# Revit family: Platinum_BC_iPlus_8_MR
name_source: partatom
category: Equipos mecánicos
units: mm (PartAtom-declared; Revit-internal decimal feet)

## family parameters
Compartido = No
Corte con vacíos al cargar = No
Cota de conector redondo = Diámetro de uso
Número OmniClass = 23.75.10.21
Punto de cálculo de habitación = No
Se basa en plano de trabajo = No
Siempre vertical = Sí
Tipo de pieza = Normal
Título OmniClass = Heat Pumps

## types (1)
- Platinum BC iPLUS 8 MR (U.E)
    Altura = 943 mm  [stored 3.09383 ft]
    Anchura = 950 mm
    Blanco = Color RGB 216-216-216
    Cantidad Compresores = 1
    Cantidad de Ventiladores = 1
    Capacidad Calorifica (kW) = 7.9
    Capacidad frigorifica (kW) = 7.9
    Caudal Aire (m3/min) = 55
    Código de montaje = 7609926
    Descripción = Platinum BC iPlus 8MR
    Diametro drenaje = 32 mm
    Diametro gas refrigerante = 15.9 mm
    Diametro liquido refrigerante = 9.53 mm
    Fabricante = BAXI
    Gris = Color RGB 100-100-100
    Hertz = 50 Hz
    IFCExportAs = IfcPumpType
    IFCExportType = NOTDEFINED
    Intensidad Máxima (A) = 19
    Modelo = Platinum BC iPlus 8MR
    Negro = Color RGB 060-060-060
    Peso Unidad (kg) = 75
    Phase = 1
    Potencia Acustical (dB(A)) = 65.2
    Profundidad = 330 mm
    Revit Version = 2016
    Rojo = Color RGB 255-000-000
    Tipo Compresor = Inverter hermetic twin rotary
    Tipo Refrigerante = R410A
    Tipo Ventilador = Propeller Fan
    URL = https://www.baxi.es
    URL PRODUCTO = https://www.baxi.es
    Voltage = 230 V

note: [stored X ft] marks values corroborated as IEEE doubles in the binary element streams (Revit-internal decimal feet)

## geometry (parser evidence)
native form markers: Blend x2, Sweep x2
no freeform markers — native parametric forms only
